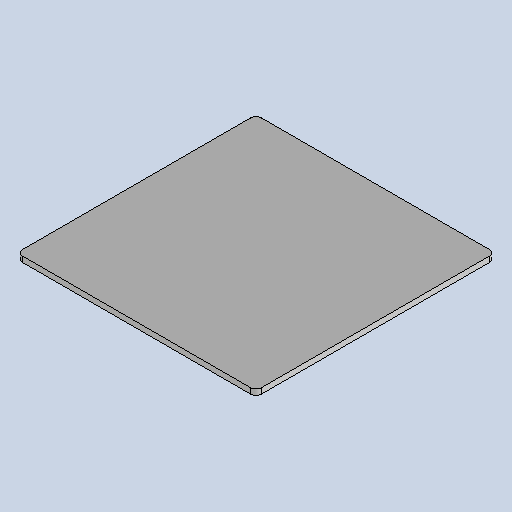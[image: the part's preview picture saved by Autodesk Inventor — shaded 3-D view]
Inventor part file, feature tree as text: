
AUTODESK INVENTOR PART (.ipt)
format: ipt  version: 2025.3 (Build 293356030, 356C)  size: 172,032 bytes
history: native  units: mm
features: other x2, sheet_metal_op x1, chamfer x1, sketch x1
ambient origin geometry x8: Origin, YZ Plane, XZ Plane, XY Plane, X Axis, Y Axis, Z Axis, Center Point
bodies: Body1 (feature_tree)
feature tree (5):
  sheet_metal_op  "Face3"
  chamfer  "Corner Round1"
  sketch  "Sketch1"  dims[d154=86.0mm d155=86.0mm d156=2.0mm d178=2.0mm]
  other  "Plate5"
  other  "Definition1"
